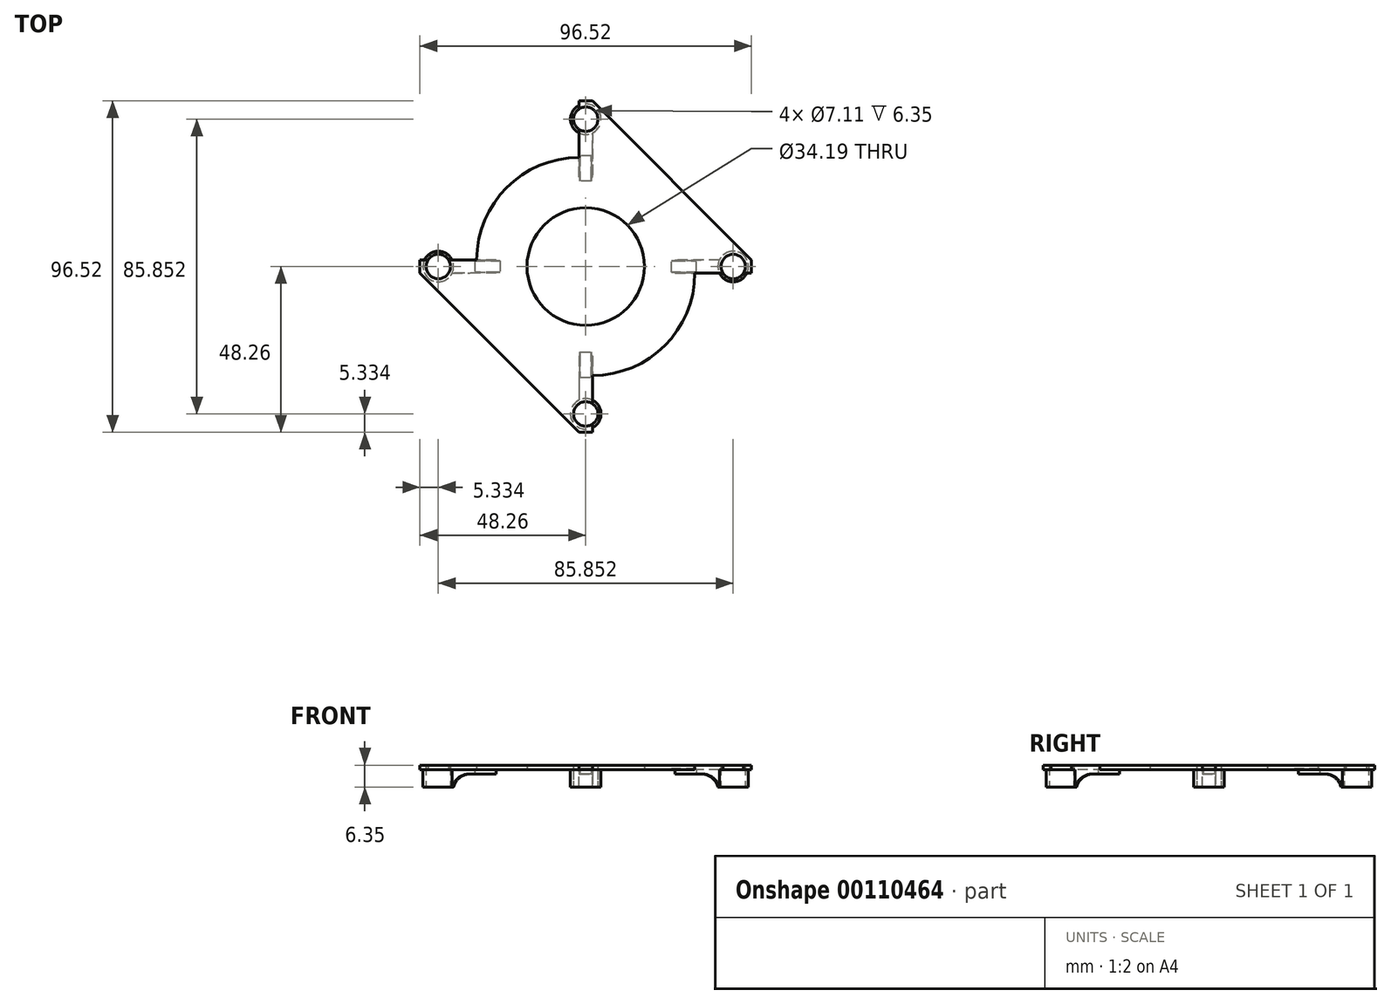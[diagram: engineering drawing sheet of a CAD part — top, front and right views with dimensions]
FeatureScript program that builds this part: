
annotation { "Feature Type Name" : "Feature", "Feature Type Description" : "" }
export const myFeature = defineFeature(function(context is Context, id is Id, definition is map)
    precondition{}
    {
        {
            var Q0;
            Q0=qCreatedBy(makeId("Top.planeOp"),FACE);
            var sketch = newSketch(context, id + "F0", { "sketchPlane" : qUnion([Q0])});
            skPoint(sketch, "E0.middle", {"position": v(0, 0) * mm});
            skLineSegment(sketch, "E1", {"start": v(-40, 4.84) * mm, "end": v(-26.04, 4.84) * mm, "construction": true});
            skLineSegment(sketch, "E2.MirrorCS", {"start": v(40, 4.84) * mm, "end": v(26.04, 4.84) * mm, "construction": true});
            skLineSegment(sketch, "E3.MirrorCS", {"start": v(-40, -4.84) * mm, "end": v(-26.04, -4.84) * mm, "construction": true});
            skLineSegment(sketch, "E4.MirrorCS", {"start": v(40, -4.84) * mm, "end": v(26.04, -4.84) * mm, "construction": true});
            skLineSegment(sketch, "E5", {"start": v(-4.78, 40) * mm, "end": v(-4.78, 26.03) * mm, "construction": true});
            skLineSegment(sketch, "E6.MirrorCS", {"start": v(4.78, 40) * mm, "end": v(4.78, 26.03) * mm, "construction": true});
            skLineSegment(sketch, "E7.MirrorCS", {"start": v(4.78, -40) * mm, "end": v(4.78, -26.03) * mm, "construction": true});
            skLineSegment(sketch, "E8.MirrorCS", {"start": v(-4.78, -40) * mm, "end": v(-4.78, -26.03) * mm, "construction": true});
            skLineSegment(sketch, "E9.bottom", {"start": v(-31.75, 1.93) * mm, "end": v(-48.26, 1.93) * mm});
            skLineSegment(sketch, "E9.top", {"start": v(-31.75, -1.93) * mm, "end": v(-48.26, -1.93) * mm});
            skLineSegment(sketch, "E9.right", {"start": v(-48.26, 1.93) * mm, "end": v(-48.26, -1.93) * mm});
            skPoint(sketch, "E9.middle", {"position": v(-40, 0) * mm});
            skLineSegment(sketch, "E10.MirrorCS", {"start": v(31.75, -1.93) * mm, "end": v(48.26, -1.93) * mm});
            skLineSegment(sketch, "E11.MirrorCS", {"start": v(31.75, 1.93) * mm, "end": v(48.26, 1.93) * mm});
            skLineSegment(sketch, "E12.MirrorCS", {"start": v(48.26, 1.93) * mm, "end": v(48.26, -1.93) * mm});
            skLineSegment(sketch, "E13.top", {"start": v(1.93, 48.26) * mm, "end": v(-1.93, 48.26) * mm});
            skLineSegment(sketch, "E13.left", {"start": v(1.93, 31.75) * mm, "end": v(1.93, 48.26) * mm});
            skLineSegment(sketch, "E13.right", {"start": v(-1.93, 31.75) * mm, "end": v(-1.93, 48.26) * mm});
            skPoint(sketch, "E13.middle", {"position": v(0, 40) * mm});
            skLineSegment(sketch, "E14.MirrorCS", {"start": v(-1.93, -31.75) * mm, "end": v(-1.93, -48.26) * mm});
            skLineSegment(sketch, "E15.MirrorCS", {"start": v(1.93, -48.26) * mm, "end": v(-1.93, -48.26) * mm});
            skLineSegment(sketch, "E16.MirrorCS", {"start": v(1.93, -31.75) * mm, "end": v(1.93, -48.26) * mm});
            skArc(sketch, "E17", {"start": v(-31.75, 1.93) * mm, "mid": v(-23.02, 23.02) * mm, "end": v(-1.93, 31.75) * mm});
            skArc(sketch, "E18", {"start": v(31.75, 1.93) * mm, "mid": v(23.02, 23.02) * mm, "end": v(1.93, 31.75) * mm});
            skArc(sketch, "E19", {"start": v(-31.75, -1.93) * mm, "mid": v(-23.02, -23.02) * mm, "end": v(-1.93, -31.75) * mm});
            skArc(sketch, "E20", {"start": v(31.75, -1.93) * mm, "mid": v(23.02, -23.02) * mm, "end": v(1.93, -31.75) * mm});
            skLineSegment(sketch, "E21", {"start": v(1.93, 48.26) * mm, "end": v(48.26, 1.93) * mm});
            skLineSegment(sketch, "E22", {"start": v(48.26, -1.93) * mm, "end": v(1.93, -48.26) * mm});
            skLineSegment(sketch, "E23", {"start": v(-1.93, -48.26) * mm, "end": v(-48.26, -1.93) * mm});
            skLineSegment(sketch, "E24", {"start": v(-48.26, 1.93) * mm, "end": v(-1.93, 48.26) * mm});
            skCircle(sketch, "E25", {"center": v(0, -42.93) * mm, "radius": 3.56 * mm});
            skCircle(sketch, "E26.MirrorC", {"center": v(0, 42.93) * mm, "radius": 3.56 * mm});
            skCircle(sketch, "E27", {"center": v(-42.93, 0) * mm, "radius": 3.56 * mm});
            skCircle(sketch, "E28.MirrorC", {"center": v(42.93, 0) * mm, "radius": 3.56 * mm});
            skLineSegment(sketch, "E29.bottom", {"start": v(-1.93, 31.75) * mm, "end": v(1.93, 31.75) * mm});
            skLineSegment(sketch, "E29.top", {"start": v(-1.93, 26.03) * mm, "end": v(1.93, 26.03) * mm});
            skLineSegment(sketch, "E29.left", {"start": v(-1.93, 31.75) * mm, "end": v(-1.93, 26.03) * mm});
            skLineSegment(sketch, "E29.right", {"start": v(1.93, 31.75) * mm, "end": v(1.93, 26.03) * mm});
            skLineSegment(sketch, "E30.bottom", {"start": v(-31.75, 1.93) * mm, "end": v(-26.04, 1.93) * mm});
            skLineSegment(sketch, "E30.top", {"start": v(-31.75, -1.93) * mm, "end": v(-26.04, -1.93) * mm});
            skLineSegment(sketch, "E30.left", {"start": v(-31.75, 1.93) * mm, "end": v(-31.75, -1.93) * mm});
            skLineSegment(sketch, "E30.right", {"start": v(-26.04, 1.93) * mm, "end": v(-26.04, -1.93) * mm});
            skLineSegment(sketch, "E31.bottom", {"start": v(31.75, 1.93) * mm, "end": v(26.04, 1.93) * mm});
            skLineSegment(sketch, "E31.top", {"start": v(31.75, -1.93) * mm, "end": v(26.04, -1.93) * mm});
            skLineSegment(sketch, "E31.left", {"start": v(31.75, 1.93) * mm, "end": v(31.75, -1.93) * mm});
            skLineSegment(sketch, "E31.right", {"start": v(26.04, 1.93) * mm, "end": v(26.04, -1.93) * mm});
            skLineSegment(sketch, "E32.bottom", {"start": v(1.93, -31.75) * mm, "end": v(-1.93, -31.75) * mm});
            skLineSegment(sketch, "E32.top", {"start": v(1.93, -26.03) * mm, "end": v(-1.93, -26.03) * mm});
            skLineSegment(sketch, "E32.left", {"start": v(1.93, -31.75) * mm, "end": v(1.93, -26.03) * mm});
            skLineSegment(sketch, "E32.right", {"start": v(-1.93, -31.75) * mm, "end": v(-1.93, -26.03) * mm});
            skCircle(sketch, "E33", {"center": v(0, 0) * mm, "radius": 17.1 * mm});
            skSolve(sketch);
        }
        {
            var Q0;
            {var subQ0=sQuery(id+"F0.wireOp",EDGE,"E19");Q0=makeQuery(id+"F0.imprint","IMPRINT",FACE,{"disambiguationData":[TD([[makeQuery(id+"F0.imprint","IMPRINT",EDGE,{"derivedFrom":subQ0}),-1.0]])]});}
            var Q1;
            {var subQ0=sQuery(id+"F0.wireOp",EDGE,"E9.right");Q1=makeQuery(id+"F0.imprint","IMPRINT",FACE,{"disambiguationData":[TD([[makeQuery(id+"F0.imprint","IMPRINT",EDGE,{"derivedFrom":subQ0}),1.0]])]});}
            var Q2;
            {var subQ4=sQuery(id+"F0.wireOp",EDGE,"E17");Q2=makeQuery(id+"F0.imprint","IMPRINT",FACE,{"disambiguationData":[TD([[makeQuery(id+"F0.imprint","IMPRINT",EDGE,{"derivedFrom":subQ4}),1.0]])]});}
            var Q3;
            {var subQ0=sQuery(id+"F0.wireOp",EDGE,"E15.MirrorCS");Q3=makeQuery(id+"F0.imprint","IMPRINT",FACE,{"disambiguationData":[TD([[makeQuery(id+"F0.imprint","IMPRINT",EDGE,{"derivedFrom":subQ0}),-1.0]])]});}
            var Q4;
            {var subQ4=sQuery(id+"F0.wireOp",EDGE,"E20");Q4=makeQuery(id+"F0.imprint","IMPRINT",FACE,{"disambiguationData":[TD([[makeQuery(id+"F0.imprint","IMPRINT",EDGE,{"derivedFrom":subQ4}),1.0]])]});}
            var Q5;
            {var subQ0=sQuery(id+"F0.wireOp",EDGE,"E12.MirrorCS");Q5=makeQuery(id+"F0.imprint","IMPRINT",FACE,{"disambiguationData":[TD([[makeQuery(id+"F0.imprint","IMPRINT",EDGE,{"derivedFrom":subQ0}),-1.0]])]});}
            var Q6;
            {var subQ8=sQuery(id+"F0.wireOp",EDGE,"E18");Q6=makeQuery(id+"F0.imprint","IMPRINT",FACE,{"disambiguationData":[TD([[makeQuery(id+"F0.imprint","IMPRINT",EDGE,{"derivedFrom":subQ8}),-1.0]])]});}
            var Q7;
            {var subQ0=sQuery(id+"F0.wireOp",EDGE,"E13.top");Q7=makeQuery(id+"F0.imprint","IMPRINT",FACE,{"disambiguationData":[TD([[makeQuery(id+"F0.imprint","IMPRINT",EDGE,{"derivedFrom":subQ0}),1.0]])]});}
            extrude(context, id + "F1", {"entities" : qUnion([Q0, Q1, Q2, Q3, Q4, Q5, Q6, Q7]), "depth" : 1.27 * mm});
        }
        {
            var Q0;
            {var subQ0=sQuery(id+"F0.wireOp",EDGE,"E31.left");Q0=makeQuery(id+"F0.imprint","IMPRINT",FACE,{"disambiguationData":[TD([[makeQuery(id+"F0.imprint","IMPRINT",EDGE,{"derivedFrom":subQ0}),1.0]])]});}
            var Q1;
            {var subQ0=sQuery(id+"F0.wireOp",EDGE,"E32.bottom");Q1=makeQuery(id+"F0.imprint","IMPRINT",FACE,{"disambiguationData":[TD([[makeQuery(id+"F0.imprint","IMPRINT",EDGE,{"derivedFrom":subQ0}),1.0]])]});}
            var Q2;
            {var subQ0=sQuery(id+"F0.wireOp",EDGE,"E30.left");Q2=makeQuery(id+"F0.imprint","IMPRINT",FACE,{"disambiguationData":[TD([[makeQuery(id+"F0.imprint","IMPRINT",EDGE,{"derivedFrom":subQ0}),-1.0]])]});}
            var Q3;
            {var subQ0=sQuery(id+"F0.wireOp",EDGE,"E29.bottom");Q3=makeQuery(id+"F0.imprint","IMPRINT",FACE,{"disambiguationData":[TD([[makeQuery(id+"F0.imprint","IMPRINT",EDGE,{"derivedFrom":subQ0}),1.0]])]});}
            var Q4;
            Q4=makeQuery(id+"F0.imprint","IMPRINT",FACE,{"disambiguationData":[TD([[makeQuery(id+"F0.imprint","IMPRINT",EDGE,{"derivedFrom":sQuery(id+"F0.wireOp",EDGE,"E32.bottom")}),-1.0]])]});
            var Q5;
            Q5=makeQuery(id+"F0.imprint","IMPRINT",FACE,{"disambiguationData":[TD([[makeQuery(id+"F0.imprint","IMPRINT",EDGE,{"derivedFrom":sQuery(id+"F0.wireOp",EDGE,"E29.bottom")}),-1.0]])]});
            var Q6;
            Q6=makeQuery(id+"F0.imprint","IMPRINT",FACE,{"disambiguationData":[TD([[makeQuery(id+"F0.imprint","IMPRINT",EDGE,{"derivedFrom":sQuery(id+"F0.wireOp",EDGE,"E31.bottom")}),1.0]])]});
            var Q7;
            Q7=makeQuery(id+"F0.imprint","IMPRINT",FACE,{"disambiguationData":[TD([[makeQuery(id+"F0.imprint","IMPRINT",EDGE,{"derivedFrom":sQuery(id+"F0.wireOp",EDGE,"E30.bottom")}),-1.0]])]});
            extrude(context, id + "F2", {"entities" : qUnion([Q0, Q1, Q2, Q3, Q4, Q5, Q6, Q7]), "operationType" : NewBodyOperationType.ADD, "depth" : 1.27 * mm, "hasSecondDirection" : true, "secondDirectionOppositeDirection" : true, "secondDirectionDepth" : 1.27 * mm});
        }
        {
            var Q0;
            Q0=makeQuery(id+"F2.opExtrude","CAP_FACE",FACE,{"disambiguationData":[OSD([sQuery(id+"F0.wireOp",EDGE,"E14.MirrorCS"),sQuery(id+"F0.wireOp",EDGE,"E16.MirrorCS"),sQuery(id+"F0.wireOp",EDGE,"E25"),sQuery(id+"F0.wireOp",EDGE,"E32.top"),sQuery(id+"F0.wireOp",EDGE,"E32.left"),sQuery(id+"F0.wireOp",EDGE,"E32.right")])],"isStart":true});
            var sketch = newSketch(context, id + "F3", { "sketchPlane" : qUnion([Q0])});
            skLineSegment(sketch, "E34.bottom", {"start": v(1.65, 32.26) * mm, "end": v(-1.65, 32.26) * mm});
            skLineSegment(sketch, "E34.top", {"start": v(1.65, 24.94) * mm, "end": v(-1.65, 24.94) * mm});
            skLineSegment(sketch, "E34.left", {"start": v(1.65, 32.26) * mm, "end": v(1.65, 24.94) * mm});
            skLineSegment(sketch, "E34.right", {"start": v(-1.65, 32.26) * mm, "end": v(-1.65, 24.94) * mm});
            skPoint(sketch, "E34.middle", {"position": v(0, 28.6) * mm});
            skLineSegment(sketch, "E35.MirrorCS", {"start": v(1.65, -24.94) * mm, "end": v(-1.65, -24.94) * mm});
            skLineSegment(sketch, "E36.MirrorCS", {"start": v(-1.65, -32.26) * mm, "end": v(-1.65, -24.94) * mm});
            skLineSegment(sketch, "E37.MirrorCS", {"start": v(1.65, -32.26) * mm, "end": v(-1.65, -32.26) * mm});
            skLineSegment(sketch, "E38.MirrorCS", {"start": v(1.65, -32.26) * mm, "end": v(1.65, -24.94) * mm});
            skSolve(sketch);
        }
        {
            var Q0;
            {var subQ0=sQuery(id+"F3.wireOp",EDGE,"E34.top");Q0=makeQuery(id+"F3.imprint","IMPRINT",FACE,{"disambiguationData":[TD([[makeQuery(id+"F3.imprint","IMPRINT",EDGE,{"derivedFrom":subQ0}),-1.0]])]});}
            var Q1;
            {var subQ0=sQuery(id+"F3.wireOp",EDGE,"E34.bottom");Q1=makeQuery(id+"F3.imprint","IMPRINT",FACE,{"disambiguationData":[TD([[makeQuery(id+"F3.imprint","IMPRINT",EDGE,{"derivedFrom":subQ0}),1.0]])]});}
            extrude(context, id + "F4", {"entities" : qUnion([Q0, Q1]), "depth" : 2.54 * mm});
        }
        {
            var Q0;
            Q0=makeQuery(id+"F4.opExtrude","SWEPT_BODY",BODY,{"disambiguationData":[OSD([sQuery(id+"F3.wireOp",EDGE,"E34.bottom"),sQuery(id+"F3.wireOp",EDGE,"E34.top"),sQuery(id+"F3.wireOp",EDGE,"E34.left"),sQuery(id+"F3.wireOp",EDGE,"E34.right")])]});
            var Q1;
            Q1=sQuery(id+"F0.wireOp",EDGE,"E33");
            circularPattern(context, id + "F5", {"entities" : qUnion([Q0]), "axis" : qUnion([Q1]), "angle" : 90 * degree, "instanceCount" : 4});
        }
        {
            var Q0;
            Q0=makeQuery(id+"F4.opExtrude","CAP_FACE",FACE,{"disambiguationData":[OSD([sQuery(id+"F3.wireOp",EDGE,"E34.bottom"),sQuery(id+"F3.wireOp",EDGE,"E34.top"),sQuery(id+"F3.wireOp",EDGE,"E34.left"),sQuery(id+"F3.wireOp",EDGE,"E34.right")])],"isStart":false});
            var Q1;
            Q1=makeQuery(id+"F5.opPattern","COPY",FACE,{"derivedFrom":makeQuery(id+"F4.opExtrude","CAP_FACE",FACE,{"disambiguationData":[OSD([sQuery(id+"F3.wireOp",EDGE,"E34.bottom"),sQuery(id+"F3.wireOp",EDGE,"E34.top"),sQuery(id+"F3.wireOp",EDGE,"E34.left"),sQuery(id+"F3.wireOp",EDGE,"E34.right")])],"isStart":false}),"instanceName":"3"});
            var Q2;
            Q2=makeQuery(id+"F5.opPattern","COPY",FACE,{"derivedFrom":makeQuery(id+"F4.opExtrude","CAP_FACE",FACE,{"disambiguationData":[OSD([sQuery(id+"F3.wireOp",EDGE,"E34.bottom"),sQuery(id+"F3.wireOp",EDGE,"E34.top"),sQuery(id+"F3.wireOp",EDGE,"E34.left"),sQuery(id+"F3.wireOp",EDGE,"E34.right")])],"isStart":false}),"instanceName":"1"});
            var Q3;
            Q3=makeQuery(id+"F5.opPattern","COPY",FACE,{"derivedFrom":makeQuery(id+"F4.opExtrude","CAP_FACE",FACE,{"disambiguationData":[OSD([sQuery(id+"F3.wireOp",EDGE,"E34.bottom"),sQuery(id+"F3.wireOp",EDGE,"E34.top"),sQuery(id+"F3.wireOp",EDGE,"E34.left"),sQuery(id+"F3.wireOp",EDGE,"E34.right")])],"isStart":false}),"instanceName":"2"});
            extrude(context, id + "F6", {"entities" : qUnion([Q0, Q1, Q2, Q3]), "operationType" : NewBodyOperationType.REMOVE, "oppositeDirection" : true, "depth" : 4.06 * mm});
        }
        {
            var Q0;
            {var subQ0=sQuery(id+"F0.wireOp",EDGE,"E19");Q0=makeQuery(id+"F0.imprint","IMPRINT",FACE,{"disambiguationData":[TD([[makeQuery(id+"F0.imprint","IMPRINT",EDGE,{"derivedFrom":subQ0}),-1.0]])]});}
            var sketch = newSketch(context, id + "F7", { "sketchPlane" : qUnion([Q0])});
            skCircle(sketch, "E39", {"center": v(0, -42.93) * mm, "radius": 4.45 * mm});
            skCircle(sketch, "E40", {"center": v(0, -42.93) * mm, "radius": 3.56 * mm});
            skCircle(sketch, "E41.MirrorC", {"center": v(0, 42.93) * mm, "radius": 4.45 * mm});
            skCircle(sketch, "E42.MirrorC", {"center": v(0, 42.93) * mm, "radius": 3.56 * mm});
            skCircle(sketch, "E43", {"center": v(-42.93, 0) * mm, "radius": 4.45 * mm});
            skCircle(sketch, "E44", {"center": v(-42.93, 0) * mm, "radius": 3.56 * mm});
            skCircle(sketch, "E45.MirrorC", {"center": v(42.93, 0) * mm, "radius": 4.45 * mm});
            skCircle(sketch, "E46.MirrorC", {"center": v(42.93, 0) * mm, "radius": 3.56 * mm});
            skSolve(sketch);
        }
        {
            var Q0;
            Q0 = qSketchRegion(id + "F7", true);
            extrude(context, id + "F8", {"entities" : qUnion([Q0]), "operationType" : NewBodyOperationType.ADD, "oppositeDirection" : true, "depth" : 5.08 * mm});
        }
        {
            var Q0;
            Q0=makeQuery(id+"F8.boolean.opBoolean","INTERSECT",EDGE,{"derivedFrom":[makeQuery(id+"F2.opExtrude","CAP_FACE",FACE,{"disambiguationData":[OSD([sQuery(id+"F0.wireOp",EDGE,"E14.MirrorCS"),sQuery(id+"F0.wireOp",EDGE,"E16.MirrorCS"),sQuery(id+"F0.wireOp",EDGE,"E25"),sQuery(id+"F0.wireOp",EDGE,"E32.top"),sQuery(id+"F0.wireOp",EDGE,"E32.left"),sQuery(id+"F0.wireOp",EDGE,"E32.right")])],"isStart":true}),makeQuery(id+"F8.opExtrude","SWEPT_FACE",FACE,{"disambiguationData":[OSD([sQuery(id+"F7.wireOp",EDGE,"E39")])]})]});
            var Q1;
            Q1=makeQuery(id+"F8.boolean.opBoolean","INTERSECT",EDGE,{"derivedFrom":[makeQuery(id+"F2.opExtrude","CAP_FACE",FACE,{"disambiguationData":[OSD([sQuery(id+"F0.wireOp",EDGE,"E10.MirrorCS"),sQuery(id+"F0.wireOp",EDGE,"E11.MirrorCS"),sQuery(id+"F0.wireOp",EDGE,"E28.MirrorC"),sQuery(id+"F0.wireOp",EDGE,"E31.bottom"),sQuery(id+"F0.wireOp",EDGE,"E31.top"),sQuery(id+"F0.wireOp",EDGE,"E31.right")])],"isStart":true}),makeQuery(id+"F8.opExtrude","SWEPT_FACE",FACE,{"disambiguationData":[OSD([sQuery(id+"F7.wireOp",EDGE,"E45.MirrorC")])]})]});
            var Q2;
            Q2=makeQuery(id+"F8.boolean.opBoolean","INTERSECT",EDGE,{"derivedFrom":[makeQuery(id+"F2.opExtrude","CAP_FACE",FACE,{"disambiguationData":[OSD([sQuery(id+"F0.wireOp",EDGE,"E13.left"),sQuery(id+"F0.wireOp",EDGE,"E13.right"),sQuery(id+"F0.wireOp",EDGE,"E26.MirrorC"),sQuery(id+"F0.wireOp",EDGE,"E29.top"),sQuery(id+"F0.wireOp",EDGE,"E29.left"),sQuery(id+"F0.wireOp",EDGE,"E29.right")])],"isStart":true}),makeQuery(id+"F8.opExtrude","SWEPT_FACE",FACE,{"disambiguationData":[OSD([sQuery(id+"F7.wireOp",EDGE,"E41.MirrorC")])]})]});
            var Q3;
            Q3=makeQuery(id+"F8.boolean.opBoolean","INTERSECT",EDGE,{"derivedFrom":[makeQuery(id+"F2.opExtrude","CAP_FACE",FACE,{"disambiguationData":[OSD([sQuery(id+"F0.wireOp",EDGE,"E9.bottom"),sQuery(id+"F0.wireOp",EDGE,"E9.top"),sQuery(id+"F0.wireOp",EDGE,"E27"),sQuery(id+"F0.wireOp",EDGE,"E30.bottom"),sQuery(id+"F0.wireOp",EDGE,"E30.top"),sQuery(id+"F0.wireOp",EDGE,"E30.right")])],"isStart":true}),makeQuery(id+"F8.opExtrude","SWEPT_FACE",FACE,{"disambiguationData":[OSD([sQuery(id+"F7.wireOp",EDGE,"E43")])]})]});
            fillet(context, id + "F9", {"entities" : qUnion([Q0, Q1, Q2, Q3]), "radius" : 5.08 * mm, "tangentPropagation" : true, "allowEdgeOverflow" : false});
        }
    });
